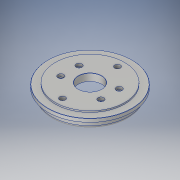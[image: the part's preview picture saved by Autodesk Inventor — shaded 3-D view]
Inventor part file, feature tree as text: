
AUTODESK INVENTOR PART (.ipt)
format: ipt  version: 2017 (Build 210142000, 142)  size: 222,208 bytes
history: native  units: in
note: dims shown in document units (in); Inventor stores cm internally (conversion verified against a paired STEP export)
features: sketch x5, hole x2, extrude x2, chamfer x2, revolve x1, fillet x1
ambient origin geometry x8: Origin, YZ Plane, XZ Plane, XY Plane, X Axis, Y Axis, Z Axis, Center Point
bodies: Solid1 (feature_tree)
feature tree (13):
  revolve  "Revolution1"  [1 undecoded]
  hole  "Hole1"  [1 undecoded]
  fillet  "Fillet1"  Radius=1.4975in
  sketch  "Sketch3"  dims[d13=90.0deg d14=2.376in]
  hole  "Hole2"  [1 undecoded]
  extrude  "Extrusion1"  Depth=0.125in
  chamfer  "Chamfer1"  Distance=1.47in
  extrude  "Extrusion2"  Depth=0.05in
  chamfer  "Chamfer2"  Distance=0.787in
  sketch  "Sketch1"  dims[d1=0.5in d3=0.147in d5=0.195in d8=0.691in d9=1.668in]
  sketch  "Sketch2"  dims[d10=1.814in d11=0.062in d12=1.4975in]
  sketch  "Sketch4"  dims[d15=0.25in d16=0.75in d17=0.375in d18=0.25in d19=0.5635in d20=0.3in d21=0.0in d22=0.125in]
  sketch  "Sketch5"  dims[d23=2.25in d24=1.47in d25=0.05in d26=0.787in d27=1.732in d28=0.134in d29=0.75in d30=0.256in d31=0.118in d32=0.5635in d33=1.0in d34=0.8108in d35=0.25in d36=0.0in d37=0.02in d38=0.125in d39=45.0deg d40=1.0in d41=0.2in d42=0.0in d43=0.01in d44=0.125in d45=45.0deg]
note: 3 required parameter values undecoded (feature->parameter linkage not recoverable at this tier; creation-order binding heuristic only, values carry confidence <= 0.55)